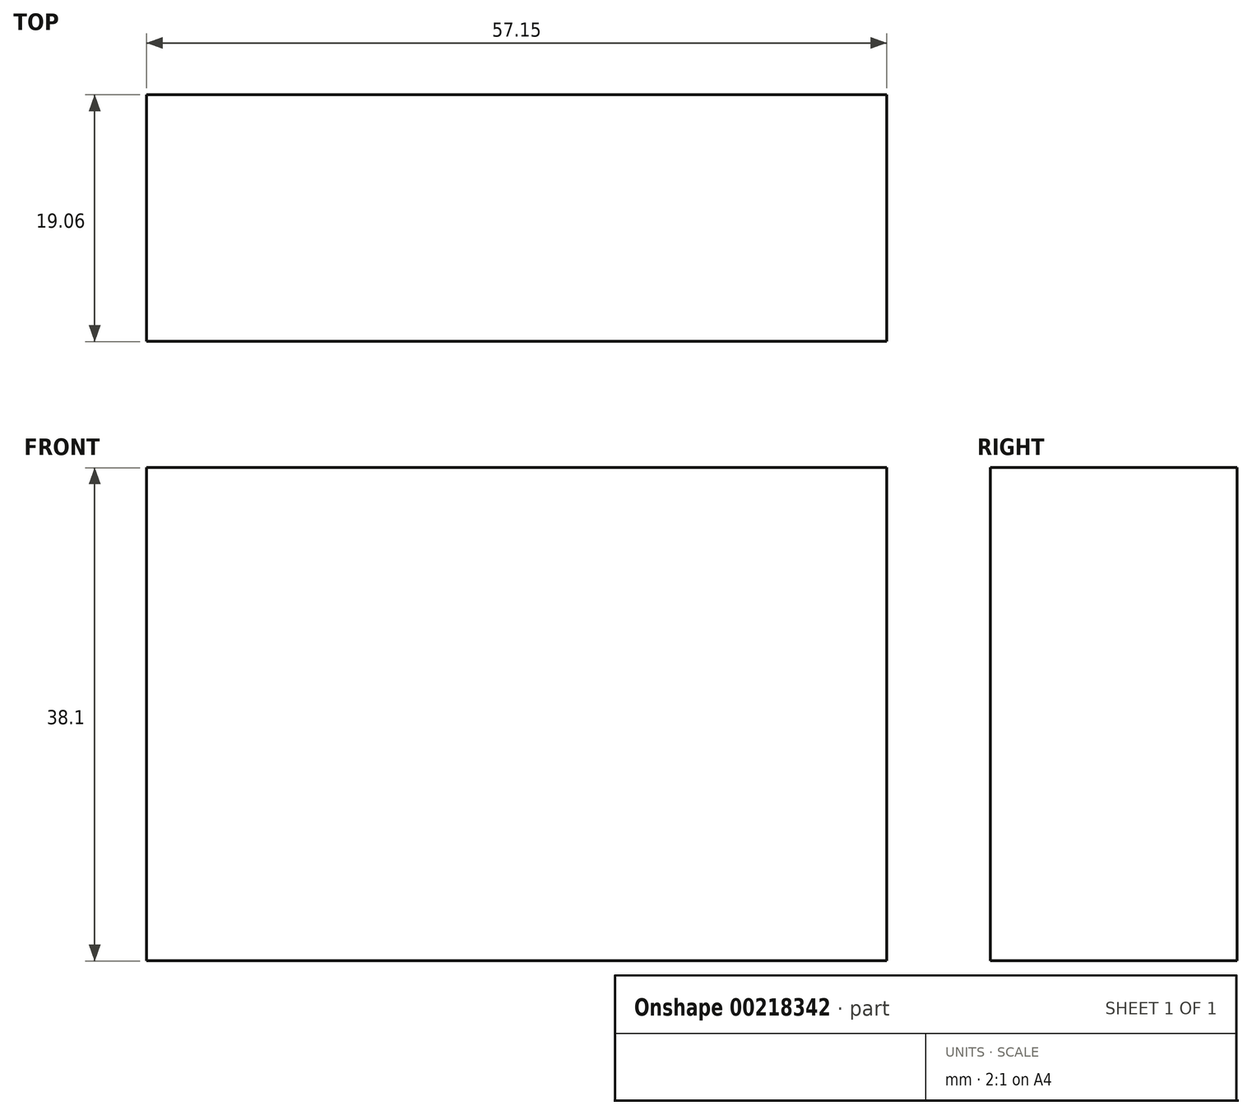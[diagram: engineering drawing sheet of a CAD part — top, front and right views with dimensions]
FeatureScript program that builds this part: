
annotation { "Feature Type Name" : "Feature", "Feature Type Description" : "" }
export const myFeature = defineFeature(function(context is Context, id is Id, definition is map)
    precondition{}
    {
        {
            var Q0;
            Q0=qCreatedBy(makeId("Front.planeOp"),FACE);
            var sketch = newSketch(context, id + "F0", { "sketchPlane" : qUnion([Q0])});
            skLineSegment(sketch, "E0.bottom", {"start": v(-9.52, 9.53) * mm, "end": v(9.53, 9.53) * mm});
            skLineSegment(sketch, "E0.top", {"start": v(-9.53, -9.53) * mm, "end": v(9.52, -9.53) * mm});
            skLineSegment(sketch, "E0.left", {"start": v(-9.52, 9.53) * mm, "end": v(-9.53, -9.53) * mm});
            skLineSegment(sketch, "E0.right", {"start": v(9.53, 9.53) * mm, "end": v(9.52, -9.53) * mm});
            skPoint(sketch, "E0.middle", {"position": v(0, 0) * mm});
            skSolve(sketch);
        }
        {
            var Q0;
            Q0 = qSketchRegion(id + "F0", true);
            extrude(context, id + "F1", {"entities" : qUnion([Q0]), "endBound" : BoundingType.SYMMETRIC, "depth" : 19.05 * mm});
        }
        {
            var Q0;
            Q0=makeQuery(id+"F1.opExtrude","SWEPT_FACE",FACE,{"disambiguationData":[OSD([sQuery(id+"F0.wireOp",EDGE,"E0.right")])]});
            extrude(context, id + "F2", {"entities" : qUnion([Q0]), "operationType" : NewBodyOperationType.ADD, "depth" : 38.1 * mm});
        }
        {
            var Q0;
            {var subQ0=sQuery(id+"F0.wireOp",EDGE,"E0.bottom");Q0=makeQuery(id+"F2.boolean.opBoolean","MERGE",FACE,{"derivedFrom":[makeQuery(id+"F1.opExtrude","SWEPT_FACE",FACE,{"disambiguationData":[OSD([subQ0])]}),makeQuery(id+"F2.opExtrude","SWEPT_FACE",FACE,{"disambiguationData":[OSD([subQ0,sQuery(id+"F0.wireOp",EDGE,"E0.right")])]})]});}
            extrude(context, id + "F3", {"entities" : qUnion([Q0]), "operationType" : NewBodyOperationType.ADD, "depth" : 19.05 * mm});
        }
    });
